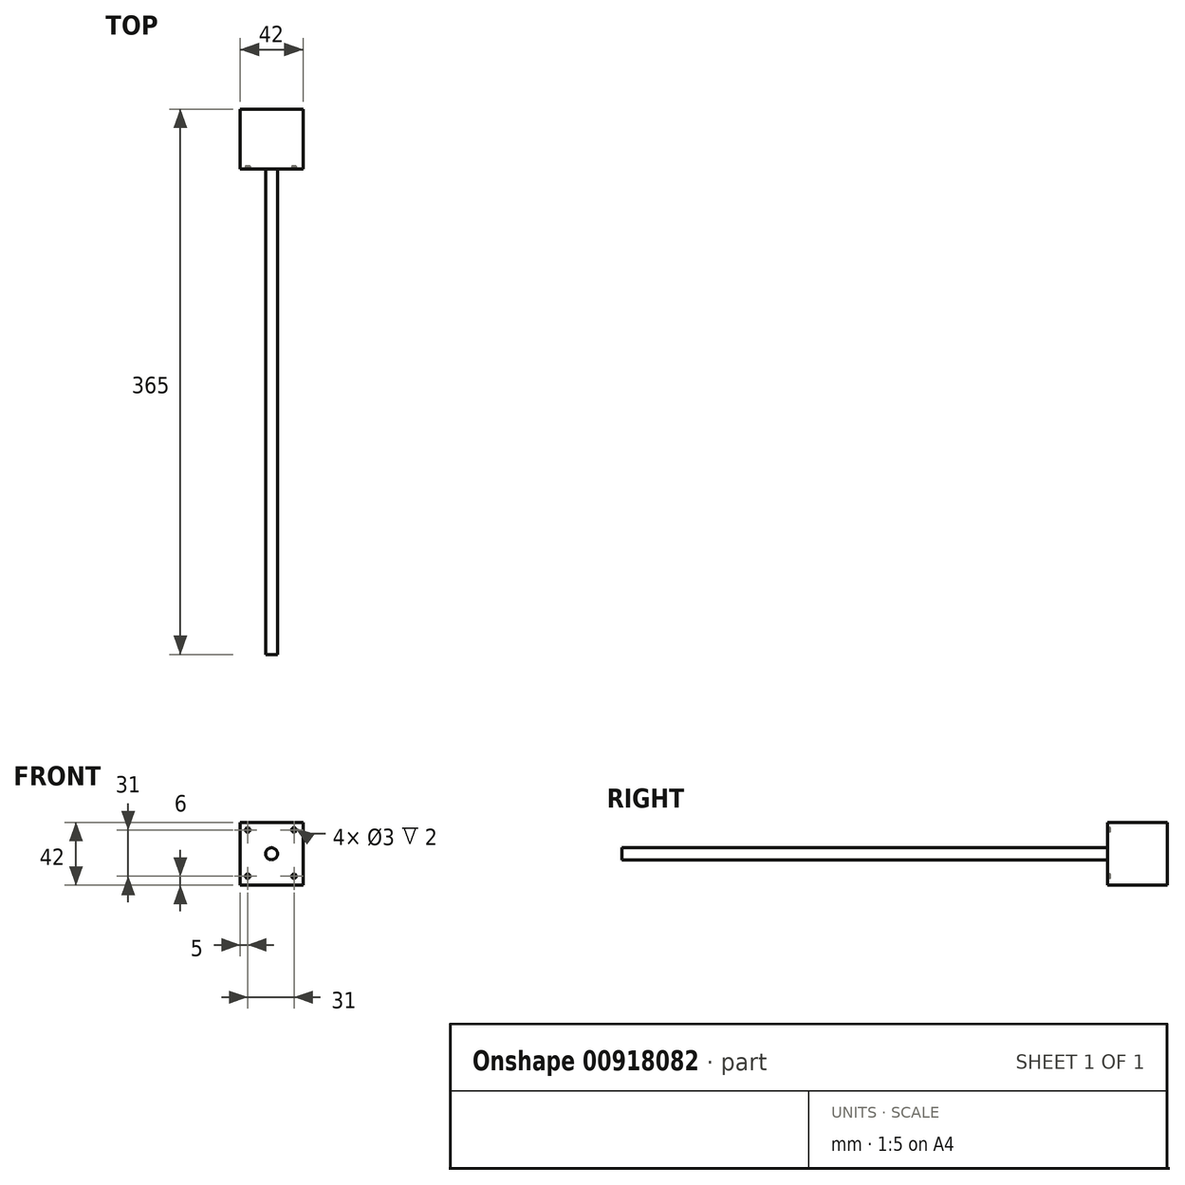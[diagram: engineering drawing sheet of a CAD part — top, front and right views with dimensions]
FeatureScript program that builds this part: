
annotation { "Feature Type Name" : "Feature", "Feature Type Description" : "" }
export const myFeature = defineFeature(function(context is Context, id is Id, definition is map)
    precondition{}
    {
        {
            var Q0;
            Q0=qCreatedBy(makeId("Front.planeOp"),FACE);
            var sketch = newSketch(context, id + "F0", { "sketchPlane" : qUnion([Q0])});
            skLineSegment(sketch, "E0.rect.bottom", {"start": v(21, -21) * mm, "end": v(-21, -21) * mm});
            skLineSegment(sketch, "E0.rect.top", {"start": v(21, 21) * mm, "end": v(-21, 21) * mm});
            skLineSegment(sketch, "E0.rect.left", {"start": v(21, -21) * mm, "end": v(21, 21) * mm});
            skLineSegment(sketch, "E0.rect.right", {"start": v(-21, -21) * mm, "end": v(-21, 21) * mm});
            skPoint(sketch, "E0.rect.middle", {"position": v(0, 0) * mm});
            skSolve(sketch);
        }
        {
            var Q0;
            Q0=qSketchRegion(id+"F0",true);
            extrude(context, id + "F1", {"entities" : qUnion([Q0]), "depth" : 40 * mm});
        }
        {
            var Q0;
            Q0=makeQuery(id+"F1.opExtrude","CAP_FACE",FACE,{"disambiguationData":[OSD([sQuery(id+"F0.wireOp",EDGE,"E0.rect.bottom"),sQuery(id+"F0.wireOp",EDGE,"E0.rect.top"),sQuery(id+"F0.wireOp",EDGE,"E0.rect.left"),sQuery(id+"F0.wireOp",EDGE,"E0.rect.right")])],"isStart":false});
            var sketch = newSketch(context, id + "F2", { "sketchPlane" : qUnion([Q0])});
            skCircle(sketch, "E1", {"center": v(0, 0) * mm, "radius": 4 * mm});
            skSolve(sketch);
        }
        {
            var Q0;
            Q0=qSketchRegion(id+"F2",true);
            extrude(context, id + "F3", {"entities" : qUnion([Q0]), "operationType" : NewBodyOperationType.ADD, "depth" : 325 * mm});
        }
        {
            var Q0;
            Q0=makeQuery(id+"F1.opExtrude","CAP_FACE",FACE,{"disambiguationData":[OSD([sQuery(id+"F0.wireOp",EDGE,"E0.rect.bottom"),sQuery(id+"F0.wireOp",EDGE,"E0.rect.top"),sQuery(id+"F0.wireOp",EDGE,"E0.rect.left"),sQuery(id+"F0.wireOp",EDGE,"E0.rect.right")])],"isStart":false});
            var sketch = newSketch(context, id + "F4", { "sketchPlane" : qUnion([Q0])});
            skLineSegment(sketch, "E2", {"start": v(-21, 21) * mm, "end": v(-21, 16) * mm});
            skLineSegment(sketch, "E3", {"start": v(-21, 16) * mm, "end": v(-16, 16) * mm});
            skLineSegment(sketch, "E4", {"start": v(-16, 16) * mm, "end": v(-16, -15) * mm, "construction": true});
            skLineSegment(sketch, "E5", {"start": v(-16, -15) * mm, "end": v(15, -15) * mm, "construction": true});
            skLineSegment(sketch, "E6", {"start": v(15, -15) * mm, "end": v(15, 16) * mm, "construction": true});
            skLineSegment(sketch, "E7", {"start": v(15, 16) * mm, "end": v(-16, 16) * mm, "construction": true});
            skCircle(sketch, "E8", {"center": v(-16, -15) * mm, "radius": 1.5 * mm});
            skCircle(sketch, "E9", {"center": v(-16, 16) * mm, "radius": 1.5 * mm});
            skCircle(sketch, "E10", {"center": v(15, -15) * mm, "radius": 1.5 * mm});
            skCircle(sketch, "E11", {"center": v(15, 16) * mm, "radius": 1.5 * mm});
            skSolve(sketch);
        }
        {
            var Q0;
            Q0=qSketchRegion(id+"F4",true);
            extrude(context, id + "F5", {"entities" : qUnion([Q0]), "operationType" : NewBodyOperationType.REMOVE, "oppositeDirection" : true, "depth" : 2 * mm});
        }
    });
